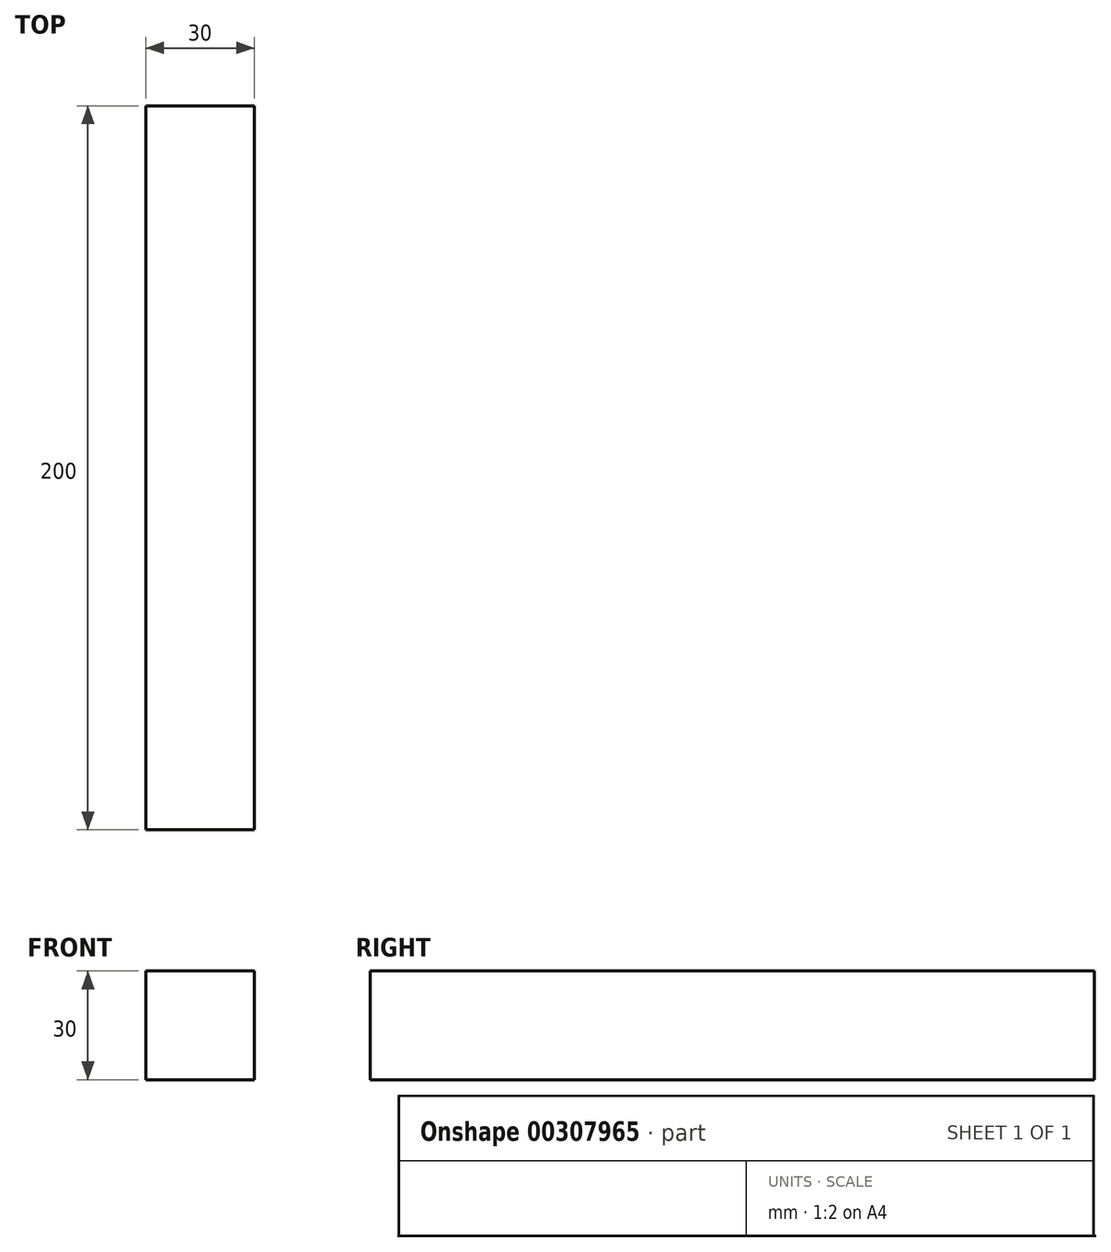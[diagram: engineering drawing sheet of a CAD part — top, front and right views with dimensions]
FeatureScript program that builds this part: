
annotation { "Feature Type Name" : "Feature", "Feature Type Description" : "" }
export const myFeature = defineFeature(function(context is Context, id is Id, definition is map)
    precondition{}
    {
        {
            var Q0;
            Q0=qCreatedBy(makeId("Front.planeOp"),FACE);
            var sketch = newSketch(context, id + "F0", { "sketchPlane" : qUnion([Q0])});
            skLineSegment(sketch, "E0.bottom", {"start": v(15, -15) * mm, "end": v(-15, -15) * mm});
            skLineSegment(sketch, "E0.top", {"start": v(15, 15) * mm, "end": v(-15, 15) * mm});
            skLineSegment(sketch, "E0.left", {"start": v(15, -15) * mm, "end": v(15, 15) * mm});
            skLineSegment(sketch, "E0.right", {"start": v(-15, -15) * mm, "end": v(-15, 15) * mm});
            skPoint(sketch, "E0.middle", {"position": v(0, 0) * mm});
            skSolve(sketch);
        }
        {
            var Q0;
            Q0=makeQuery(id+"F0.imprint","IMPRINT",FACE,{"disambiguationData":[TD([[makeQuery(id+"F0.imprint","IMPRINT",EDGE,{"derivedFrom":sQuery(id+"F0.wireOp",EDGE,"E0.bottom")}),-1.0]])]});
            extrude(context, id + "F1", {"entities" : qUnion([Q0]), "endBound" : BoundingType.SYMMETRIC, "depth" : 200 * mm});
        }
    });
